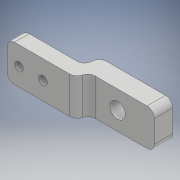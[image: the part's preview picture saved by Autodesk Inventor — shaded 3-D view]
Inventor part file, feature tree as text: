
AUTODESK INVENTOR PART (.ipt)
format: ipt  version: 2018 (Build 220112000, 112)  size: 146,432 bytes
history: native  units: mm
features: extrude x3, sketch x3, fillet x2
ambient origin geometry x8: Origin, YZ Plane, XZ Plane, XY Plane, X Axis, Y Axis, Z Axis, Center Point
bodies: Solid1 (feature_tree)
feature tree (8):
  extrude  "Extrusion1"  Depth=4.0mm
  extrude  "Extrusion2"  Depth=10.0mm TaperAngle=0.0deg
  fillet  "Fillet1"  Radius=4.2mm
  extrude  "Extrusion3"  Depth=10.0mm TaperAngle=0.0deg
  fillet  "Fillet2"  Radius=2.0mm
  sketch  "Sketch1"  dims[d0=5.0mm d2=4.0mm]
  sketch  "Sketch2"  dims[d3=20.0mm d5=10.0mm d6=0.0mm d7=4.2mm]
  sketch  "Sketch3"  dims[d8=10.0mm d9=10.0mm d10=0.0mm d11=2.0mm d13=19.0mm d14=2.0mm d15=4.0mm d17=2.3mm d18=6.5mm d19=5.1mm d20=3.25mm d21=10.0mm d22=0.0mm d23=2.0mm]
